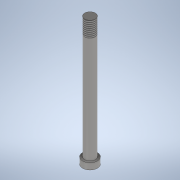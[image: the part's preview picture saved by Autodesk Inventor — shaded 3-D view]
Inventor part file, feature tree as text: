
AUTODESK INVENTOR PART (.ipt)
format: ipt  version: 2022 (Build 260153000, 153)  size: 114,688 bytes
history: native  units: in
note: dims shown in document units (in); Inventor stores cm internally (conversion verified against a paired STEP export)
features: extrude x3, sketch x3, thread x1
ambient origin geometry x8: Origin, YZ Plane, XZ Plane, XY Plane, X Axis, Y Axis, Z Axis, Center Point
bodies: Solid1 (feature_tree)
feature tree (7):
  extrude  "Extrusion1"  Depth=2.2835in TaperAngle=0.0deg
  extrude  "Extrusion2"  Depth=0.1181in TaperAngle=0.0deg
  thread  "Thread1"  [1 undecoded]
  extrude  "Extrusion3"  [1 undecoded]
  sketch  "Sketch1"  dims[d0=0.1969in d1=2.2835in d2=0.0in]
  sketch  "Sketch2"  dims[d3=0.2756in d4=0.1181in d5=0.0in d6=0.2953in d7=0.0in]
  sketch  "Sketch3"  dims[d9=0.0394in d10=0.0in]
note: 2 required parameter values undecoded (feature->parameter linkage not recoverable at this tier; creation-order binding heuristic only, values carry confidence <= 0.55)
